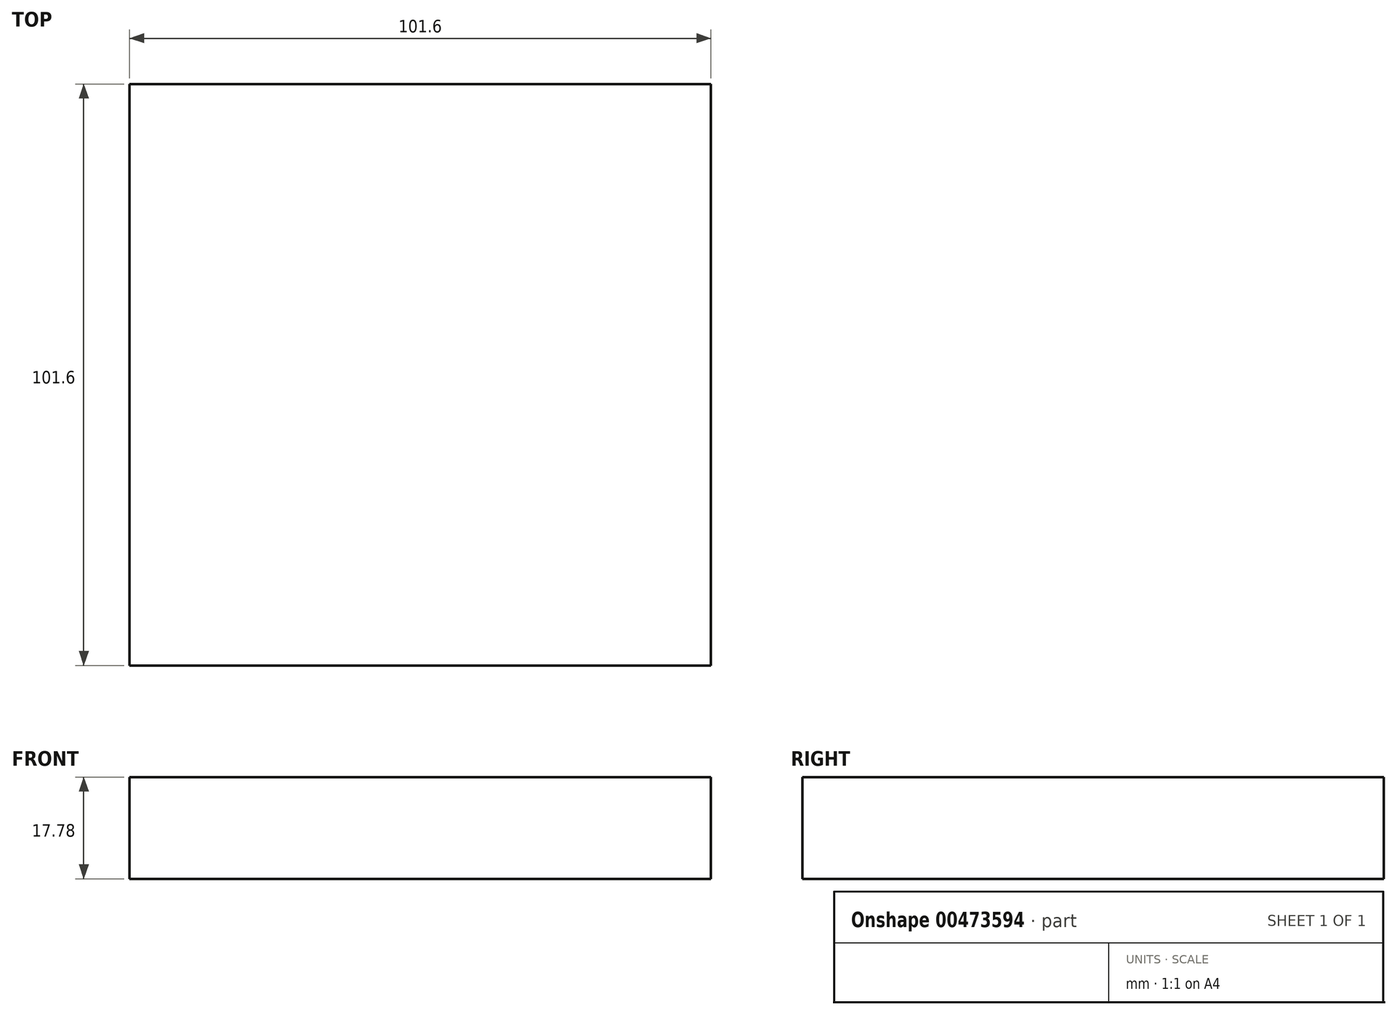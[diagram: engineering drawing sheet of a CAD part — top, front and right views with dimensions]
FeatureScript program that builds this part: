
annotation { "Feature Type Name" : "Feature", "Feature Type Description" : "" }
export const myFeature = defineFeature(function(context is Context, id is Id, definition is map)
    precondition{}
    {
        {
            var Q0;
            Q0=qCreatedBy(makeId("Front.planeOp"),FACE);
            var sketch = newSketch(context, id + "F0", { "sketchPlane" : qUnion([Q0])});
            skLineSegment(sketch, "E0.bottom", {"start": v(-53.34, 0) * mm, "end": v(48.26, 0) * mm});
            skLineSegment(sketch, "E0.top", {"start": v(-53.34, 0) * mm, "end": v(48.26, 0) * mm});
            skLineSegment(sketch, "E0.left", {"start": v(-53.34, 0) * mm, "end": v(-53.34, 0) * mm});
            skLineSegment(sketch, "E0.right", {"start": v(48.26, 0) * mm, "end": v(48.26, 0) * mm});
            skLineSegment(sketch, "E1", {"start": v(-53.34, 0) * mm, "end": v(-53.34, 17.78) * mm});
            skLineSegment(sketch, "E2", {"start": v(48.26, 0) * mm, "end": v(48.26, 17.78) * mm});
            skLineSegment(sketch, "E3", {"start": v(-53.34, 17.78) * mm, "end": v(48.26, 17.78) * mm});
            skSolve(sketch);
        }
        {
            var Q0;
            Q0 = qSketchRegion(id + "F0", true);
            extrude(context, id + "F1", {"entities" : qUnion([Q0]), "depth" : 101.6 * mm});
        }
    });
